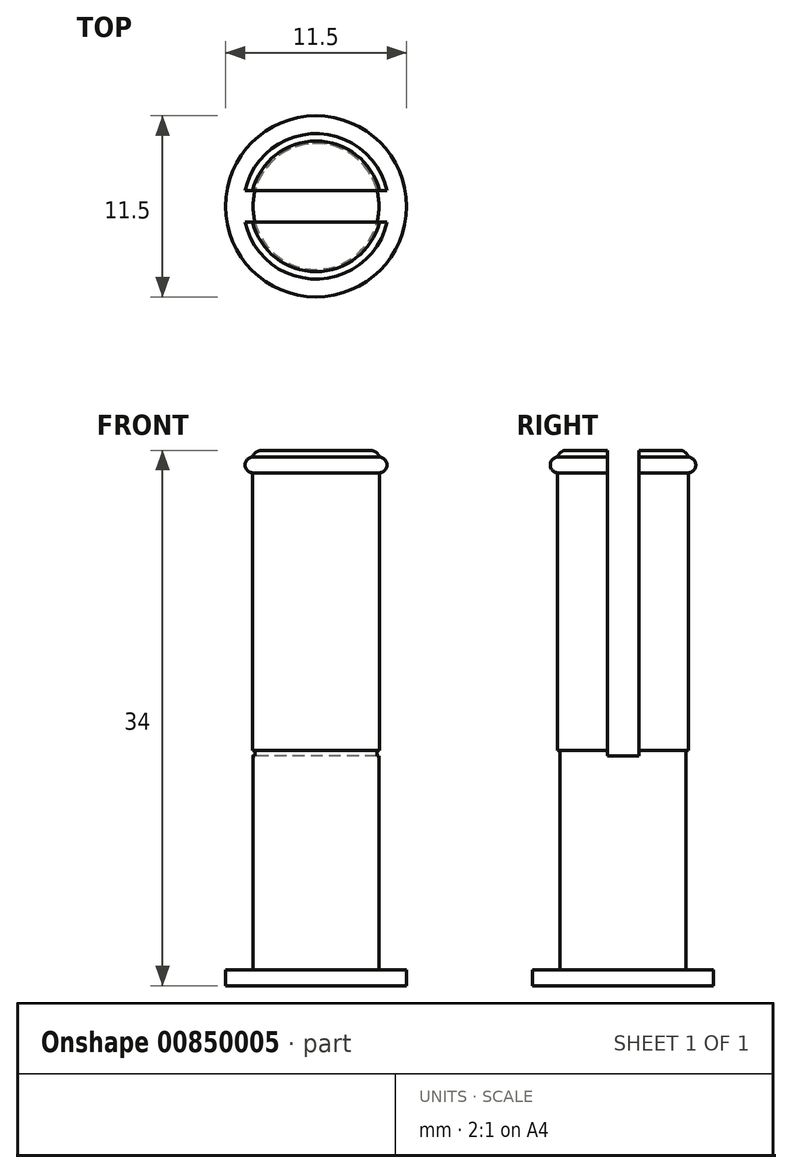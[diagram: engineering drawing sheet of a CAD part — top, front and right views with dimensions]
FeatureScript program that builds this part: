
annotation { "Feature Type Name" : "Feature", "Feature Type Description" : "" }
export const myFeature = defineFeature(function(context is Context, id is Id, definition is map)
    precondition{}
    {
        {
            var Q0;
            Q0=qCreatedBy(makeId("Top.planeOp"),FACE);
            var sketch = newSketch(context, id + "F0", { "sketchPlane" : qUnion([Q0])});
            skCircle(sketch, "E0", {"center": v(0, 0) * mm, "radius": 5.75 * mm});
            skSolve(sketch);
        }
        {
            var Q0;
            Q0 = qSketchRegion(id + "F0", true);
            extrude(context, id + "F1", {"entities" : qUnion([Q0]), "depth" : 1 * mm, "offsetDistance" : 25.4 * mm});
        }
        {
            var Q0;
            Q0=makeQuery(id+"F1.opExtrude","CAP_FACE",FACE,{"disambiguationData":[OSD([sQuery(id+"F0.wireOp",EDGE,"E0")])],"isStart":false});
            var sketch = newSketch(context, id + "F2", { "sketchPlane" : qUnion([Q0])});
            skCircle(sketch, "E1", {"center": v(0, 0) * mm, "radius": 4 * mm});
            skSolve(sketch);
        }
        {
            var Q0;
            Q0 = qSketchRegion(id + "F2", true);
            extrude(context, id + "F3", {"entities" : qUnion([Q0]), "operationType" : NewBodyOperationType.ADD, "depth" : 33 * mm, "offsetDistance" : 25.4 * mm});
        }
        {
            var Q0;
            Q0=makeQuery(id+"F3.opExtrude","CAP_FACE",FACE,{"disambiguationData":[OSD([sQuery(id+"F2.wireOp",EDGE,"E1")])],"isStart":false});
            var sketch = newSketch(context, id + "F4", { "sketchPlane" : qUnion([Q0])});
            skCircle(sketch, "E2", {"center": v(0, 0) * mm, "radius": 4.15 * mm});
            skSolve(sketch);
        }
        {
            var Q0;
            Q0 = qSketchRegion(id + "F4", true);
            extrude(context, id + "F5", {"entities" : qUnion([Q0]), "operationType" : NewBodyOperationType.ADD, "oppositeDirection" : true, "depth" : 19.05 * mm, "offsetDistance" : 25.4 * mm});
        }
        {
            var Q0;
            Q0=qCreatedBy(makeId("Front.planeOp"),FACE);
            var sketch = newSketch(context, id + "F6", { "sketchPlane" : qUnion([Q0])});
            skCircle(sketch, "E3", {"center": v(4.12, 33.07) * mm, "radius": 0.5 * mm});
            skLineSegment(sketch, "E4", {"start": v(0, 34.95) * mm, "end": v(0, 31.38) * mm, "construction": true});
            skSolve(sketch);
        }
        {
            var Q0;
            Q0=makeQuery(id+"F6.imprint","IMPRINT",FACE,{"disambiguationData":[TD([[makeQuery(id+"F6.imprint","IMPRINT",EDGE,{"derivedFrom":sQuery(id+"F6.wireOp",EDGE,"E3")}),1.0]])]});
            var Q1;
            Q1=sQuery(id+"F6.wireOp",EDGE,"E3");
            var Q2;
            Q2=sQuery(id+"F6.wireOp",EDGE,"E4");
            revolve(context, id + "F7", {"operationType" : NewBodyOperationType.ADD, "surfaceOperationType" : NewSurfaceOperationType.ADD, "entities" : qUnion([Q0]), "surfaceEntities" : qUnion([Q1]), "axis" : qUnion([Q2]), "revolveType" : RevolveType.FULL});
        }
        {
            var Q0;
            Q0=makeQuery(id+"F5.opExtrude","CAP_EDGE",EDGE,{"disambiguationData":[OSD([sQuery(id+"F4.wireOp",EDGE,"E2")])],"isStart":true});
            fillet(context, id + "F8", {"entities" : qUnion([Q0]), "radius" : 0.55 * mm, "tangentPropagation" : true, "allowEdgeOverflow" : false});
        }
        {
            var Q0;
            Q0=makeQuery(id+"F5.boolean.opBoolean","MERGE",FACE,{"derivedFrom":[makeQuery(id+"F3.opExtrude","CAP_FACE",FACE,{"disambiguationData":[OSD([sQuery(id+"F2.wireOp",EDGE,"E1")])],"isStart":false}),makeQuery(id+"F5.opExtrude","CAP_FACE",FACE,{"disambiguationData":[OSD([sQuery(id+"F4.wireOp",EDGE,"E2")])],"isStart":true})]});
            var sketch = newSketch(context, id + "F9", { "sketchPlane" : qUnion([Q0])});
            skLineSegment(sketch, "E5.bottom", {"start": v(9.9, -1) * mm, "end": v(-9.9, -1) * mm});
            skLineSegment(sketch, "E5.top", {"start": v(9.9, 1) * mm, "end": v(-9.9, 1) * mm});
            skLineSegment(sketch, "E5.left", {"start": v(9.9, -1) * mm, "end": v(9.9, 1) * mm});
            skLineSegment(sketch, "E5.right", {"start": v(-9.9, -1) * mm, "end": v(-9.9, 1) * mm});
            skPoint(sketch, "E5.middle", {"position": v(0, 0) * mm});
            skSolve(sketch);
        }
        {
            var Q0;
            Q0 = qSketchRegion(id + "F9", true);
            extrude(context, id + "F10", {"entities" : qUnion([Q0]), "operationType" : NewBodyOperationType.REMOVE, "oppositeDirection" : true, "depth" : 19.4 * mm, "offsetDistance" : 25.4 * mm});
        }
    });
